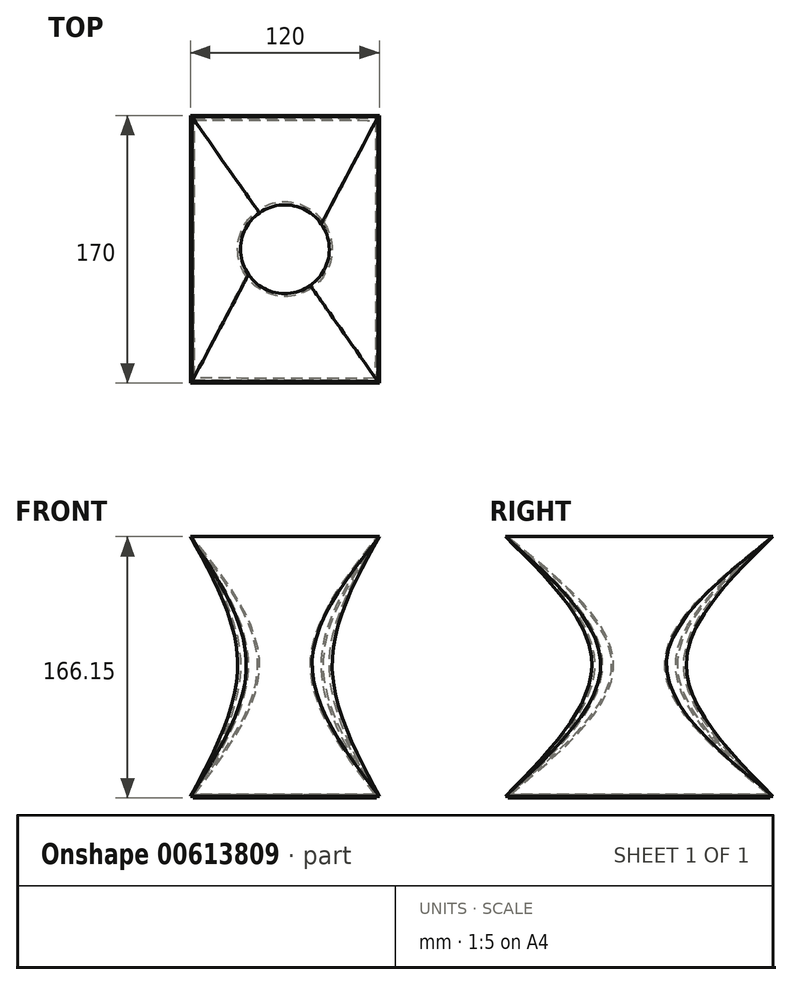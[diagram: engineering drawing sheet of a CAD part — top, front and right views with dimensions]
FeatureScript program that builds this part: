
annotation { "Feature Type Name" : "Feature", "Feature Type Description" : "" }
export const myFeature = defineFeature(function(context is Context, id is Id, definition is map)
    precondition{}
    {
        {
            var Q0;
            Q0=qCreatedBy(makeId("Top.planeOp"),FACE);
            var sketch = newSketch(context, id + "F0", { "sketchPlane" : qUnion([Q0])});
            skLineSegment(sketch, "E0.bottom", {"start": v(-60, 85) * mm, "end": v(60, 85) * mm});
            skLineSegment(sketch, "E0.top", {"start": v(-60, -85) * mm, "end": v(60, -85) * mm});
            skLineSegment(sketch, "E0.left", {"start": v(-60, 85) * mm, "end": v(-60, -85) * mm});
            skLineSegment(sketch, "E0.right", {"start": v(60, 85) * mm, "end": v(60, -85) * mm});
            skPoint(sketch, "E0.middle", {"position": v(0, 0) * mm});
            skSolve(sketch);
        }
        {
            var Q0;
            Q0=qCreatedBy(makeId("Top.planeOp"),FACE);
            var sketch = newSketch(context, id + "F1", { "sketchPlane" : qUnion([Q0])});
            skLineSegment(sketch, "E1.bottom", {"start": v(-58.2, 83.2) * mm, "end": v(58.2, 83.2) * mm});
            skLineSegment(sketch, "E1.top", {"start": v(-58.2, -83.2) * mm, "end": v(58.2, -83.2) * mm});
            skLineSegment(sketch, "E1.left", {"start": v(-58.2, 83.2) * mm, "end": v(-58.2, -83.2) * mm});
            skLineSegment(sketch, "E1.right", {"start": v(58.2, 83.2) * mm, "end": v(58.2, -83.2) * mm});
            skPoint(sketch, "E1.middle", {"position": v(0, 0) * mm});
            skSolve(sketch);
        }
        {
            var Q0;
            Q0=qCreatedBy(makeId("Top.planeOp"),FACE);
            cPlane(context, id + "F2", {"entities" : qUnion([Q0]), "cplaneType" : CPlaneType.OFFSET, "offset" : 85 * mm, "width" : 150 * mm, "height" : 150 * mm});
        }
        {
            var Q0;
            Q0=qCreatedBy(makeId("Top.planeOp"),FACE);
            cPlane(context, id + "F3", {"entities" : qUnion([Q0]), "cplaneType" : CPlaneType.OFFSET, "offset" : 165 * mm, "width" : 150 * mm, "height" : 150 * mm});
        }
        {
            var Q0;
            Q0=qCreatedBy(id+"F2.planeOp",FACE);
            var sketch = newSketch(context, id + "F4", { "sketchPlane" : qUnion([Q0])});
            skCircle(sketch, "E2", {"center": v(0, 0) * mm, "radius": 28.2 * mm});
            skSolve(sketch);
        }
        {
            var Q0;
            Q0=qCreatedBy(id+"F2.planeOp",FACE);
            var sketch = newSketch(context, id + "F5", { "sketchPlane" : qUnion([Q0])});
            skCircle(sketch, "E3", {"center": v(0, 0) * mm, "radius": 30 * mm});
            skSolve(sketch);
        }
        {
            var Q0;
            Q0=qCreatedBy(id+"F3.planeOp",FACE);
            var sketch = newSketch(context, id + "F6", { "sketchPlane" : qUnion([Q0])});
            skLineSegment(sketch, "E4.bottom", {"start": v(-60, 85) * mm, "end": v(60, 85) * mm});
            skLineSegment(sketch, "E4.top", {"start": v(-60, -85) * mm, "end": v(60, -85) * mm});
            skLineSegment(sketch, "E4.left", {"start": v(-60, 85) * mm, "end": v(-60, -85) * mm});
            skLineSegment(sketch, "E4.right", {"start": v(60, 85) * mm, "end": v(60, -85) * mm});
            skPoint(sketch, "E4.middle", {"position": v(0, 0) * mm});
            skSolve(sketch);
        }
        {
            var Q0;
            Q0=qCreatedBy(id+"F3.planeOp",FACE);
            var sketch = newSketch(context, id + "F7", { "sketchPlane" : qUnion([Q0])});
            skLineSegment(sketch, "E5.bottom", {"start": v(-59.1, 84.1) * mm, "end": v(59.1, 84.1) * mm});
            skLineSegment(sketch, "E5.top", {"start": v(-59.1, -84.1) * mm, "end": v(59.1, -84.1) * mm});
            skLineSegment(sketch, "E5.left", {"start": v(-59.1, 84.1) * mm, "end": v(-59.1, -84.1) * mm});
            skLineSegment(sketch, "E5.right", {"start": v(59.1, 84.1) * mm, "end": v(59.1, -84.1) * mm});
            skPoint(sketch, "E5.middle", {"position": v(0, 0) * mm});
            skSolve(sketch);
        }
        {
            var Q0;
            Q0=makeQuery(id+"F0.imprint","IMPRINT",FACE,{"disambiguationData":[TD([[makeQuery(id+"F0.imprint","IMPRINT",EDGE,{"derivedFrom":sQuery(id+"F0.wireOp",EDGE,"E0.bottom")}),-1.0]])]});
            var Q1;
            Q1=makeQuery(id+"F5.imprint","IMPRINT",FACE,{"disambiguationData":[TD([[makeQuery(id+"F5.imprint","IMPRINT",EDGE,{"derivedFrom":sQuery(id+"F5.wireOp",EDGE,"E3")}),1.0]])]});
            var Q2;
            Q2=makeQuery(id+"F6.imprint","IMPRINT",FACE,{"disambiguationData":[TD([[makeQuery(id+"F6.imprint","IMPRINT",EDGE,{"derivedFrom":sQuery(id+"F6.wireOp",EDGE,"E4.bottom")}),-1.0]])]});
            loft(context, id + "F8", {"sheetProfilesArray" : [{ "sheetProfileEntities" : qUnion([Q0]) }, { "sheetProfileEntities" : qUnion([Q1]) }, { "sheetProfileEntities" : qUnion([Q2]) }]});
        }
        {
            var Q0;
            Q0=makeQuery(id+"F1.imprint","IMPRINT",FACE,{"disambiguationData":[TD([[makeQuery(id+"F1.imprint","IMPRINT",EDGE,{"derivedFrom":sQuery(id+"F1.wireOp",EDGE,"E1.bottom")}),-1.0]])]});
            var Q1;
            Q1=makeQuery(id+"F4.imprint","IMPRINT",FACE,{"disambiguationData":[TD([[makeQuery(id+"F4.imprint","IMPRINT",EDGE,{"derivedFrom":sQuery(id+"F4.wireOp",EDGE,"E2")}),1.0]])]});
            var Q2;
            Q2=makeQuery(id+"F7.imprint","IMPRINT",FACE,{"disambiguationData":[TD([[makeQuery(id+"F7.imprint","IMPRINT",EDGE,{"derivedFrom":sQuery(id+"F7.wireOp",EDGE,"E5.bottom")}),-1.0]])]});
            loft(context, id + "F9", {"sheetProfilesArray" : [{ "sheetProfileEntities" : qUnion([Q0]) }, { "sheetProfileEntities" : qUnion([Q1]) }, { "sheetProfileEntities" : qUnion([Q2]) }]});
        }
        {
            var Q0;
            Q0=makeQuery(id+"F9.opLoft","SWEPT_BODY",BODY,{"disambiguationData":[OSD([makeQuery(id+"F1.imprint","IMPRINT",FACE,{"disambiguationData":[TD([[makeQuery(id+"F1.imprint","IMPRINT",EDGE,{"derivedFrom":sQuery(id+"F1.wireOp",EDGE,"E1.bottom")}),-1.0]])]}),sQuery(id+"F4.wireOp",EDGE,"E2"),makeQuery(id+"F7.imprint","IMPRINT",FACE,{"disambiguationData":[TD([[makeQuery(id+"F7.imprint","IMPRINT",EDGE,{"derivedFrom":sQuery(id+"F7.wireOp",EDGE,"E5.bottom")}),-1.0]])]})])]});
            var Q1;
            Q1=makeQuery(id+"F8.opLoft","SWEPT_BODY",BODY,{"disambiguationData":[OSD([makeQuery(id+"F0.imprint","IMPRINT",FACE,{"disambiguationData":[TD([[makeQuery(id+"F0.imprint","IMPRINT",EDGE,{"derivedFrom":sQuery(id+"F0.wireOp",EDGE,"E0.bottom")}),-1.0]])]}),sQuery(id+"F5.wireOp",EDGE,"E3"),makeQuery(id+"F6.imprint","IMPRINT",FACE,{"disambiguationData":[TD([[makeQuery(id+"F6.imprint","IMPRINT",EDGE,{"derivedFrom":sQuery(id+"F6.wireOp",EDGE,"E4.bottom")}),-1.0]])]})])]});
            booleanBodies(context, id + "F10", {"operationType" : BooleanOperationType.SUBTRACTION, "tools" : qUnion([Q0]), "targets" : qUnion([Q1])});
        }
        {
            var Q0;
            Q0=makeQuery(id+"F1.imprint","IMPRINT",FACE,{"disambiguationData":[TD([[makeQuery(id+"F1.imprint","IMPRINT",EDGE,{"derivedFrom":sQuery(id+"F1.wireOp",EDGE,"E1.bottom")}),-1.0]])]});
            extrude(context, id + "F11", {"entities" : qUnion([Q0]), "operationType" : NewBodyOperationType.ADD, "endBound" : BoundingType.SYMMETRIC, "depth" : 2.3 * mm, "offsetDistance" : 25 * mm});
        }
    });
